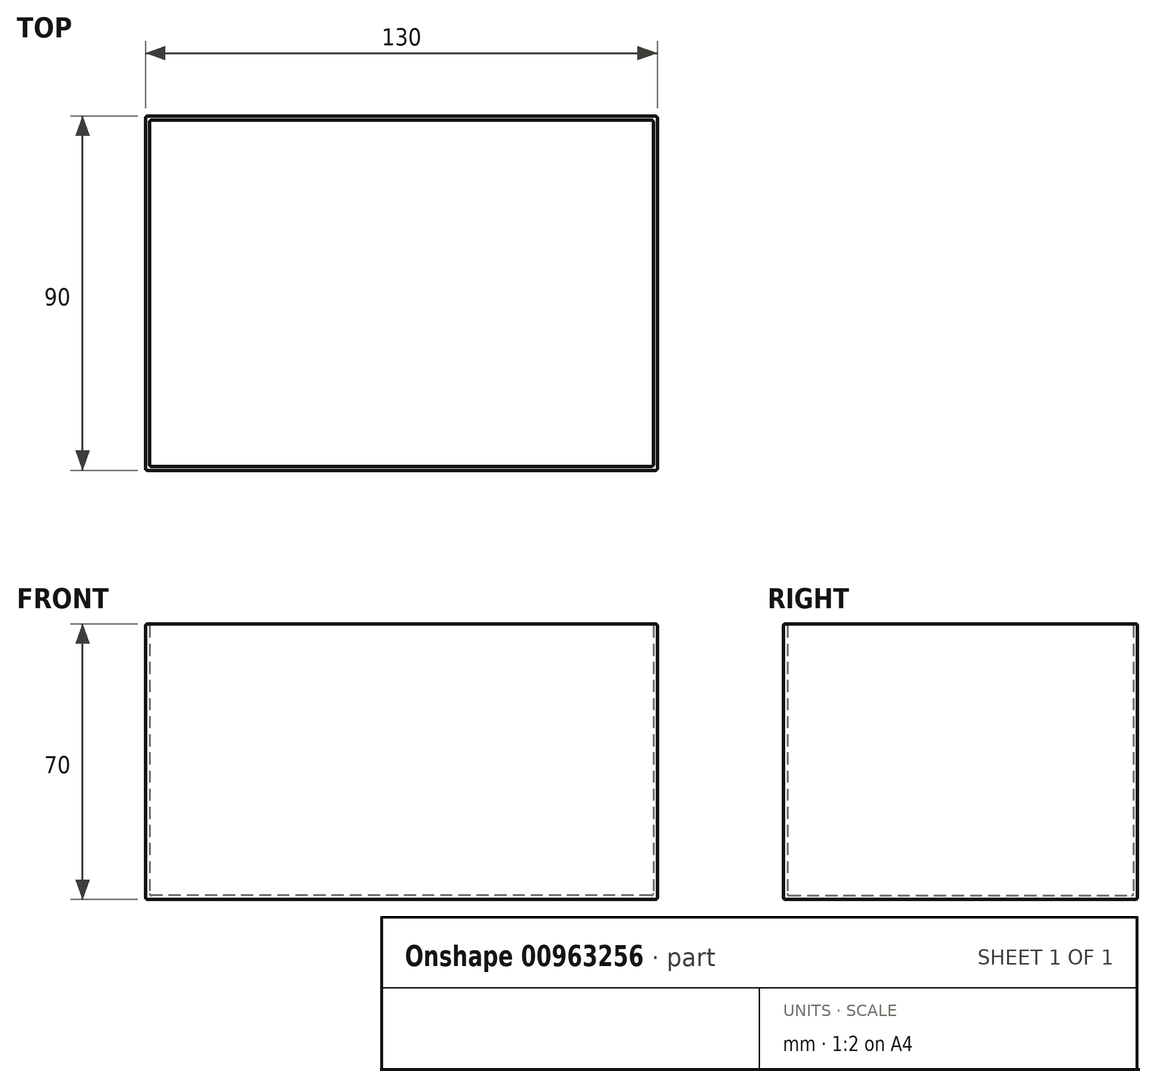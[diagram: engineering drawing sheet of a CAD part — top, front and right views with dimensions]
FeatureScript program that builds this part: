
annotation { "Feature Type Name" : "Feature", "Feature Type Description" : "" }
export const myFeature = defineFeature(function(context is Context, id is Id, definition is map)
    precondition{}
    {
        {
            var Q0;
            Q0=qCreatedBy(makeId("Top.planeOp"),FACE);
            var sketch = newSketch(context, id + "F0", { "sketchPlane" : qUnion([Q0])});
            skLineSegment(sketch, "E0.bottom", {"start": v(65, -45) * mm, "end": v(-65, -45) * mm});
            skLineSegment(sketch, "E0.top", {"start": v(65, 45) * mm, "end": v(-65, 45) * mm});
            skLineSegment(sketch, "E0.left", {"start": v(65, -45) * mm, "end": v(65, 45) * mm});
            skLineSegment(sketch, "E0.right", {"start": v(-65, -45) * mm, "end": v(-65, 45) * mm});
            skPoint(sketch, "E0.middle", {"position": v(0, 0) * mm});
            skSolve(sketch);
        }
        {
            var Q0;
            Q0=makeQuery(id+"F0.imprint","IMPRINT",FACE,{"disambiguationData":[TD([[makeQuery(id+"F0.imprint","IMPRINT",EDGE,{"derivedFrom":sQuery(id+"F0.wireOp",EDGE,"E0.bottom")}),-1.0]])]});
            extrude(context, id + "F1", {"entities" : qUnion([Q0]), "depth" : 70 * mm, "offsetDistance" : 25 * mm});
        }
        {
            var Q0;
            Q0=makeQuery(id+"F1.opExtrude","CAP_FACE",FACE,{"disambiguationData":[OSD([sQuery(id+"F0.wireOp",EDGE,"E0.bottom"),sQuery(id+"F0.wireOp",EDGE,"E0.top"),sQuery(id+"F0.wireOp",EDGE,"E0.left"),sQuery(id+"F0.wireOp",EDGE,"E0.right")])],"isStart":false});
            shell(context, id + "F2", {"entities" : qUnion([Q0]), "thickness" : 1 * mm});
        }
        {
            var Q0;
            Q0=makeQuery(id+"F1.opExtrude","SWEPT_FACE",FACE,{"disambiguationData":[OSD([sQuery(id+"F0.wireOp",EDGE,"E0.bottom")])]});
            var Q1;
            Q1=makeQuery(id+"F1.opExtrude","SWEPT_FACE",FACE,{"disambiguationData":[OSD([sQuery(id+"F0.wireOp",EDGE,"E0.right")])]});
            var Q2;
            Q2=makeQuery(id+"F1.opExtrude","SWEPT_EDGE",EDGE,{"disambiguationData":[OSD([sQuery(id+"F0.wireOp",EDGE,"E0.bottom"),sQuery(id+"F0.wireOp",EDGE,"E0.right")])]});
            var Q3;
            Q3=makeQuery(id+"F1.opExtrude","SWEPT_EDGE",EDGE,{"disambiguationData":[OSD([sQuery(id+"F0.wireOp",EDGE,"E0.bottom"),sQuery(id+"F0.wireOp",EDGE,"E0.left")])]});
            var Q4;
            Q4=makeQuery(id+"F1.opExtrude","SWEPT_EDGE",EDGE,{"disambiguationData":[OSD([sQuery(id+"F0.wireOp",EDGE,"E0.top"),sQuery(id+"F0.wireOp",EDGE,"E0.right")])]});
            var Q5;
            Q5=makeQuery(id+"F1.opExtrude","CAP_EDGE",EDGE,{"disambiguationData":[OSD([sQuery(id+"F0.wireOp",EDGE,"E0.bottom")])],"isStart":true});
            var Q6;
            Q6=makeQuery(id+"F1.opExtrude","CAP_EDGE",EDGE,{"disambiguationData":[OSD([sQuery(id+"F0.wireOp",EDGE,"E0.right")])],"isStart":true});
            var Q7;
            Q7=makeQuery(id+"F1.opExtrude","SWEPT_EDGE",EDGE,{"disambiguationData":[OSD([sQuery(id+"F0.wireOp",EDGE,"E0.top"),sQuery(id+"F0.wireOp",EDGE,"E0.left")])]});
            var Q8;
            Q8=makeQuery(id+"F2.opShell","OFFSET_EDGE",EDGE,{"disambiguationData":[OSD([sQuery(id+"F0.wireOp",EDGE,"E0.top"),sQuery(id+"F0.wireOp",EDGE,"E0.left")])]});
            var Q9;
            Q9=makeQuery(id+"F2.opShell","OFFSET_EDGE",EDGE,{"disambiguationData":[OSD([sQuery(id+"F0.wireOp",EDGE,"E0.top"),sQuery(id+"F0.wireOp",EDGE,"E0.right")])]});
            var Q10;
            {var subQ0=sQuery(id+"F0.wireOp",EDGE,"E0.right");Q10=makeQuery(id+"F2.opShell","OFFSET_EDGE",EDGE,{"disambiguationData":[OSD([subQ0]),TDD([makeQuery(id+"F1.opExtrude","CAP_EDGE",EDGE,{"disambiguationData":[OSD([subQ0])],"isStart":false})])]});}
            var Q11;
            {var subQ0=sQuery(id+"F0.wireOp",EDGE,"E0.right");Q11=makeQuery(id+"F2.opShell","OFFSET_EDGE",EDGE,{"disambiguationData":[OSD([subQ0]),TDD([makeQuery(id+"F1.opExtrude","CAP_EDGE",EDGE,{"disambiguationData":[OSD([subQ0])],"isStart":true})])]});}
            var Q12;
            Q12=makeQuery(id+"F1.opExtrude","CAP_EDGE",EDGE,{"disambiguationData":[OSD([sQuery(id+"F0.wireOp",EDGE,"E0.top")])],"isStart":false});
            var Q13;
            Q13=makeQuery(id+"F1.opExtrude","CAP_EDGE",EDGE,{"disambiguationData":[OSD([sQuery(id+"F0.wireOp",EDGE,"E0.left")])],"isStart":true});
            var Q14;
            Q14=makeQuery(id+"F1.opExtrude","CAP_EDGE",EDGE,{"disambiguationData":[OSD([sQuery(id+"F0.wireOp",EDGE,"E0.right")])],"isStart":false});
            var Q15;
            Q15=makeQuery(id+"F1.opExtrude","CAP_EDGE",EDGE,{"disambiguationData":[OSD([sQuery(id+"F0.wireOp",EDGE,"E0.bottom")])],"isStart":false});
            var Q16;
            Q16=makeQuery(id+"F1.opExtrude","CAP_EDGE",EDGE,{"disambiguationData":[OSD([sQuery(id+"F0.wireOp",EDGE,"E0.left")])],"isStart":false});
            var Q17;
            Q17=makeQuery(id+"F1.opExtrude","CAP_EDGE",EDGE,{"disambiguationData":[OSD([sQuery(id+"F0.wireOp",EDGE,"E0.top")])],"isStart":true});
            var Q18;
            Q18=makeQuery(id+"F2.opShell","OFFSET_EDGE",EDGE,{"disambiguationData":[OSD([sQuery(id+"F0.wireOp",EDGE,"E0.bottom"),sQuery(id+"F0.wireOp",EDGE,"E0.left")])]});
            var Q19;
            Q19=makeQuery(id+"F2.opShell","OFFSET_EDGE",EDGE,{"disambiguationData":[OSD([sQuery(id+"F0.wireOp",EDGE,"E0.bottom"),sQuery(id+"F0.wireOp",EDGE,"E0.right")])]});
            var Q20;
            {var subQ0=sQuery(id+"F0.wireOp",EDGE,"E0.bottom");Q20=makeQuery(id+"F2.opShell","OFFSET_EDGE",EDGE,{"disambiguationData":[OSD([subQ0]),TDD([makeQuery(id+"F1.opExtrude","CAP_EDGE",EDGE,{"disambiguationData":[OSD([subQ0])],"isStart":true})])]});}
            var Q21;
            {var subQ0=sQuery(id+"F0.wireOp",EDGE,"E0.bottom");Q21=makeQuery(id+"F2.opShell","OFFSET_EDGE",EDGE,{"disambiguationData":[OSD([subQ0]),TDD([makeQuery(id+"F1.opExtrude","CAP_EDGE",EDGE,{"disambiguationData":[OSD([subQ0])],"isStart":false})])]});}
            var Q22;
            {var subQ0=sQuery(id+"F0.wireOp",EDGE,"E0.top");Q22=makeQuery(id+"F2.opShell","OFFSET_EDGE",EDGE,{"disambiguationData":[OSD([subQ0]),TDD([makeQuery(id+"F1.opExtrude","CAP_EDGE",EDGE,{"disambiguationData":[OSD([subQ0])],"isStart":true})])]});}
            var Q23;
            {var subQ0=sQuery(id+"F0.wireOp",EDGE,"E0.top");Q23=makeQuery(id+"F2.opShell","OFFSET_EDGE",EDGE,{"disambiguationData":[OSD([subQ0]),TDD([makeQuery(id+"F1.opExtrude","CAP_EDGE",EDGE,{"disambiguationData":[OSD([subQ0])],"isStart":false})])]});}
            var Q24;
            {var subQ0=sQuery(id+"F0.wireOp",EDGE,"E0.left");Q24=makeQuery(id+"F2.opShell","OFFSET_EDGE",EDGE,{"disambiguationData":[OSD([subQ0]),TDD([makeQuery(id+"F1.opExtrude","CAP_EDGE",EDGE,{"disambiguationData":[OSD([subQ0])],"isStart":true})])]});}
            var Q25;
            {var subQ0=sQuery(id+"F0.wireOp",EDGE,"E0.left");Q25=makeQuery(id+"F2.opShell","OFFSET_EDGE",EDGE,{"disambiguationData":[OSD([subQ0]),TDD([makeQuery(id+"F1.opExtrude","CAP_EDGE",EDGE,{"disambiguationData":[OSD([subQ0])],"isStart":false})])]});}
            fillet(context, id + "F3", {"entities" : qUnion([Q0, Q1, Q2, Q3, Q4, Q5, Q6, Q7, Q8, Q9, Q10, Q11, Q12, Q13, Q14, Q15, Q16, Q17, Q18, Q19, Q20, Q21, Q22, Q23, Q24, Q25]), "radius" : .5 * mm, "tangentPropagation" : true, "allowEdgeOverflow" : false});
        }
    });
